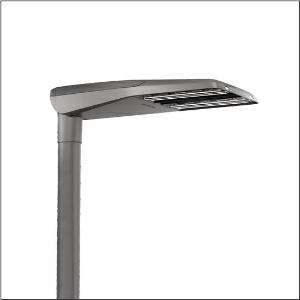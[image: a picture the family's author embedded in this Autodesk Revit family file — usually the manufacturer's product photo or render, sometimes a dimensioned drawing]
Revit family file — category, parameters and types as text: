
# Revit family: streetlight_sl_11_iq_midi___pc-r_5xc3f51e08me_15a1
name_source: partatom
category: Lighting Fixtures
units: mm (PartAtom-declared; Revit-internal decimal feet)

## family parameters
Cut with Voids When Loaded = No
Host = Face
Light Source = No
Part Type = Normal
Room Calculation Point = No
Round Connector Dimension = Use Diameter
Shared = No

## types (1)
- --- (1 x LED, 15540 lm, 124.7 W, 3000K)
    Apparent Load = 125 VA
    CIE Flux Codes = 37 73 96 100 100
    Color Rendering = 70
    Color Temperature = 3000K
    Default Elevation = 1800 mm
    Description = Streetlight SL 11 iQ midi, mast luminaire, primary light control with 3 zone facetted reflector, of plastic, silver coated, highly specular, primary optical cover: cover, of PMMA, transparent, light distribution: PC-R, light emission: direct distribution, primary light characteristic: asymmetric, right, installation type: post-top, side-entry, LED, High Power LED, rated luminous flux: 15.540lm, luminous efficacy: 125lm/W, light colour: 730, colour temperature: 3000K, control: optimised constant luminous flux control (CLO 2.0), Desk-Remote (wireless, voltage-free reading and setting of iQ features in the workshop via application-optimized NFC function/RFID function), Light-Fading, Smart-Wire, Night-Set, Lumen-Switch, Temp-Guard, Auto-Match, with cable H07RN-F 5x 1.5mm², mains connection: 230..240V, AC, 50/60Hz, connection cable pre-assembled, cable length: 12,5m, start of lifetime: 125W, end of service life: 132W, reduction: 57W, luminaire housing, of diecast aluminium, powder-coated, Siteco® metallic grey (DB 702S), please order mast flange separately, inclination adjustable without tools: 0°, 5°, 10°, 15° (post-top) | 0°, -5°, -10°, -15° (side-entry), sealing non-destructively replaceable, multi-level sealing system, length: 780mm, width: 376mm, height: 118mm, mast flange for spigot size: 42mm (side-entry): 5XC10008XM4, 60/48mm (side-entry/post-top): 5XC10108XM2, 76/60mm (side-entry/post-top): 5XC10108XM1, equipment: Power, protection rating (complete): IP66, insulation class (complete): insulation class II (safety insulation), certification: CE, ENEC, VDE, impact resistance: IK09, permissible operating ambient temperature for outdoor applications: -25..+50°C, standard-compliant lighting for roads and squares, Environmental Product Declaration (EPD) tested and certified by an independent institute, packaging unit: 1 piece

Light Distribution: PC-R
    Height = 118 mm
    Lamp = 1 x LED
    Lamp Light Flux = 15540 lm
    Lamp Power = 124.7 W
    Lamp count = 1
    Length = 780 mm
    Luminous efficacy = 125 lm/W
    Manufacturer = Siteco
    ModVariant = No
    Model = 5XC3F51E08ME
    Number of Poles = 1
    OnlyDefault = Yes
    Power Factor = 1
    Product Name = Streetlight SL 11 iQ midi | PC-R
    Product group = mast luminaire | pylon top
    ProductGroupID = 6100
    Protection Class = Protection class II
    Protection Degree = IP 66
    RLX_Detail_Level = 1
    RLX_Emergency_Light_Flux = 0 lm
    RLX_Emergency_Type = 0
    RLX_Emergency_Type_DB = No
    RlxData = <blob elided: 74445 chars, md5=51c2e072>
    Socket = socket
    Standby Power = 0 W
    System Light Flux = 15540 lm
    System Power = 125 W
    Type Comments = factory setting: luminous flux: 100 % | dim-lin: 254 | 557 mA
    Type Image = l_1005960.jpg
    URL = http://relux.com
    VarID = @adj_149047
    Voltage = 0 V
    Weight = 0.00 kg
    Width = 376 mm

## geometry (parser evidence)
native form markers: Blend x4, Sweep x10
no freeform markers — native parametric forms only
